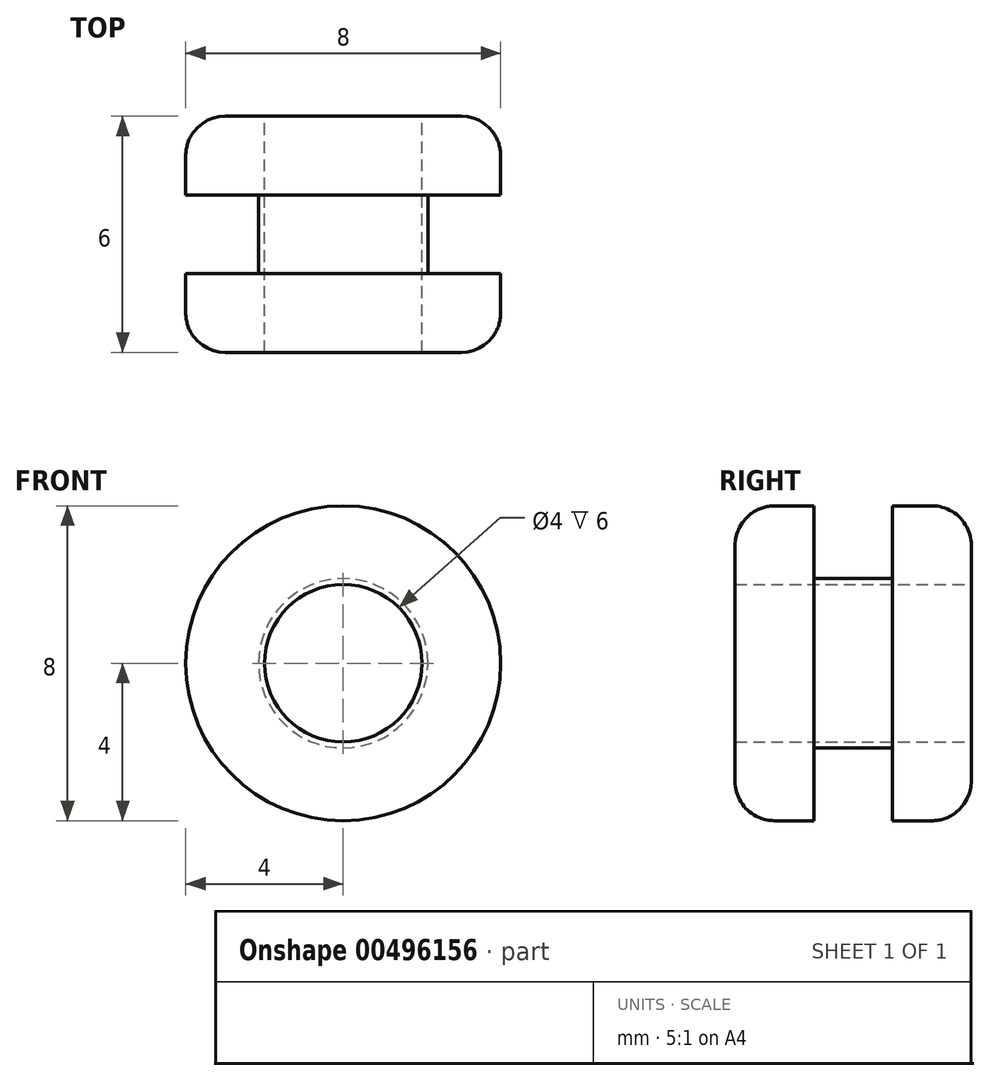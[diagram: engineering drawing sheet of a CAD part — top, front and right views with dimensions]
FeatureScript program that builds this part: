
annotation { "Feature Type Name" : "Feature", "Feature Type Description" : "" }
export const myFeature = defineFeature(function(context is Context, id is Id, definition is map)
    precondition{}
    {
        {
            var Q0;
            Q0=qCreatedBy(makeId("Front.planeOp"),FACE);
            var sketch = newSketch(context, id + "F0", { "sketchPlane" : qUnion([Q0])});
            skCircle(sketch, "E0", {"center": v(0, 0) * mm, "radius": 4 * mm});
            skSolve(sketch);
        }
        {
            var Q0;
            Q0 = qSketchRegion(id + "F0", true);
            extrude(context, id + "F1", {"entities" : qUnion([Q0]), "depth" : 2 * mm});
        }
        {
            var Q0;
            Q0=makeQuery(id+"F1.opExtrude","CAP_EDGE",EDGE,{"disambiguationData":[OSD([sQuery(id+"F0.wireOp",EDGE,"E0")])],"isStart":false});
            fillet(context, id + "F2", {"entities" : qUnion([Q0]), "radius" : 1 * mm, "tangentPropagation" : true, "allowEdgeOverflow" : false});
        }
        {
            var Q0;
            Q0=makeQuery(id+"F1.opExtrude","CAP_FACE",FACE,{"disambiguationData":[OSD([sQuery(id+"F0.wireOp",EDGE,"E0")])],"isStart":true});
            var sketch = newSketch(context, id + "F3", { "sketchPlane" : qUnion([Q0])});
            skCircle(sketch, "E1", {"center": v(0, 0) * mm, "radius": 2.15 * mm});
            skSolve(sketch);
        }
        {
            var Q0;
            Q0 = qSketchRegion(id + "F3", true);
            extrude(context, id + "F4", {"entities" : qUnion([Q0]), "operationType" : NewBodyOperationType.ADD, "depth" : 2 * mm});
        }
        {
            var Q0;
            Q0=makeQuery(id+"F4.opExtrude","CAP_FACE",FACE,{"disambiguationData":[OSD([sQuery(id+"F3.wireOp",EDGE,"E1")])],"isStart":false});
            var sketch = newSketch(context, id + "F5", { "sketchPlane" : qUnion([Q0])});
            skCircle(sketch, "E2", {"center": v(0, 0) * mm, "radius": 4 * mm});
            skSolve(sketch);
        }
        {
            var Q0;
            Q0 = qSketchRegion(id + "F5", true);
            extrude(context, id + "F6", {"entities" : qUnion([Q0]), "operationType" : NewBodyOperationType.ADD, "depth" : 2 * mm});
        }
        {
            var Q0;
            Q0=makeQuery(id+"F6.opExtrude","CAP_EDGE",EDGE,{"disambiguationData":[OSD([sQuery(id+"F5.wireOp",EDGE,"E2")])],"isStart":false});
            fillet(context, id + "F7", {"entities" : qUnion([Q0]), "radius" : 1 * mm, "tangentPropagation" : true, "allowEdgeOverflow" : false});
        }
        {
            var Q0;
            Q0=makeQuery(id+"F6.opExtrude","CAP_FACE",FACE,{"disambiguationData":[OSD([sQuery(id+"F5.wireOp",EDGE,"E2")])],"isStart":false});
            var sketch = newSketch(context, id + "F8", { "sketchPlane" : qUnion([Q0])});
            skCircle(sketch, "E3", {"center": v(0, 0) * mm, "radius": 2 * mm});
            skSolve(sketch);
        }
        {
            var Q0;
            Q0 = qSketchRegion(id + "F8", true);
            extrude(context, id + "F9", {"entities" : qUnion([Q0]), "operationType" : NewBodyOperationType.REMOVE, "oppositeDirection" : true, "depth" : 6 * mm});
        }
    });
